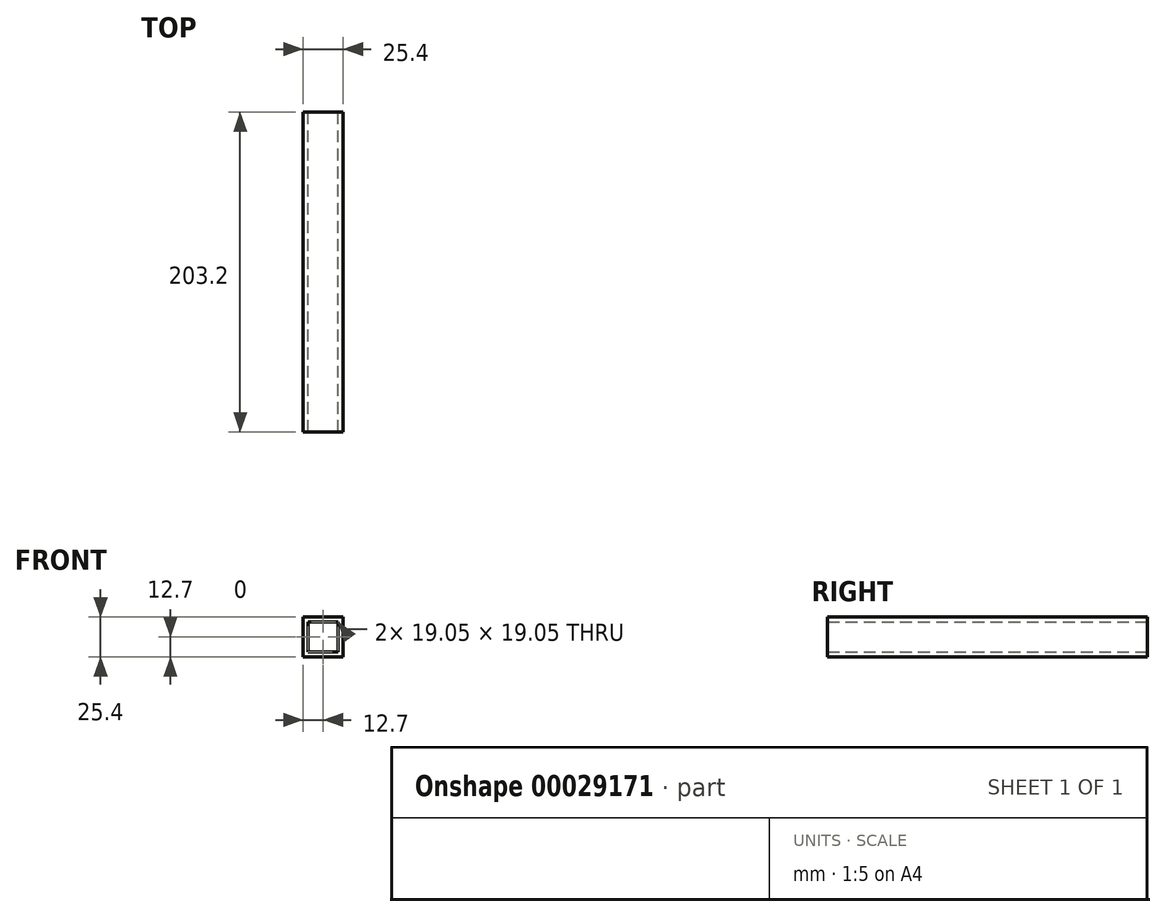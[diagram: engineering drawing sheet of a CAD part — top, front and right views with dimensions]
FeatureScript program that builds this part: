
annotation { "Feature Type Name" : "Feature", "Feature Type Description" : "" }
export const myFeature = defineFeature(function(context is Context, id is Id, definition is map)
    precondition{}
    {
        {
            var Q0;
            Q0=qCreatedBy(makeId("Front.planeOp"),FACE);
            var sketch = newSketch(context, id + "F0", { "sketchPlane" : qUnion([Q0])});
            skLineSegment(sketch, "E0.rect.bottom", {"start": v(12.7, -12.7) * mm, "end": v(-12.7, -12.7) * mm});
            skLineSegment(sketch, "E0.rect.top", {"start": v(12.7, 12.7) * mm, "end": v(-12.7, 12.7) * mm});
            skLineSegment(sketch, "E0.rect.left", {"start": v(12.7, -12.7) * mm, "end": v(12.7, 12.7) * mm});
            skLineSegment(sketch, "E0.rect.right", {"start": v(-12.7, -12.7) * mm, "end": v(-12.7, 12.7) * mm});
            skPoint(sketch, "E0.rect.middle", {"position": v(0, 0) * mm});
            skLineSegment(sketch, "E1.rect.bottom", {"start": v(9.53, -9.53) * mm, "end": v(-9.52, -9.53) * mm});
            skLineSegment(sketch, "E1.rect.top", {"start": v(9.52, 9.53) * mm, "end": v(-9.53, 9.52) * mm});
            skLineSegment(sketch, "E1.rect.left", {"start": v(9.53, -9.53) * mm, "end": v(9.52, 9.53) * mm});
            skLineSegment(sketch, "E1.rect.right", {"start": v(-9.52, -9.53) * mm, "end": v(-9.53, 9.52) * mm});
            skSolve(sketch);
        }
        {
            var Q0;
            Q0 = qSketchRegion(id + "F0", true);
            extrude(context, id + "F1", {"entities" : qUnion([Q0]), "depth" : 203.2 * mm});
        }
    });
